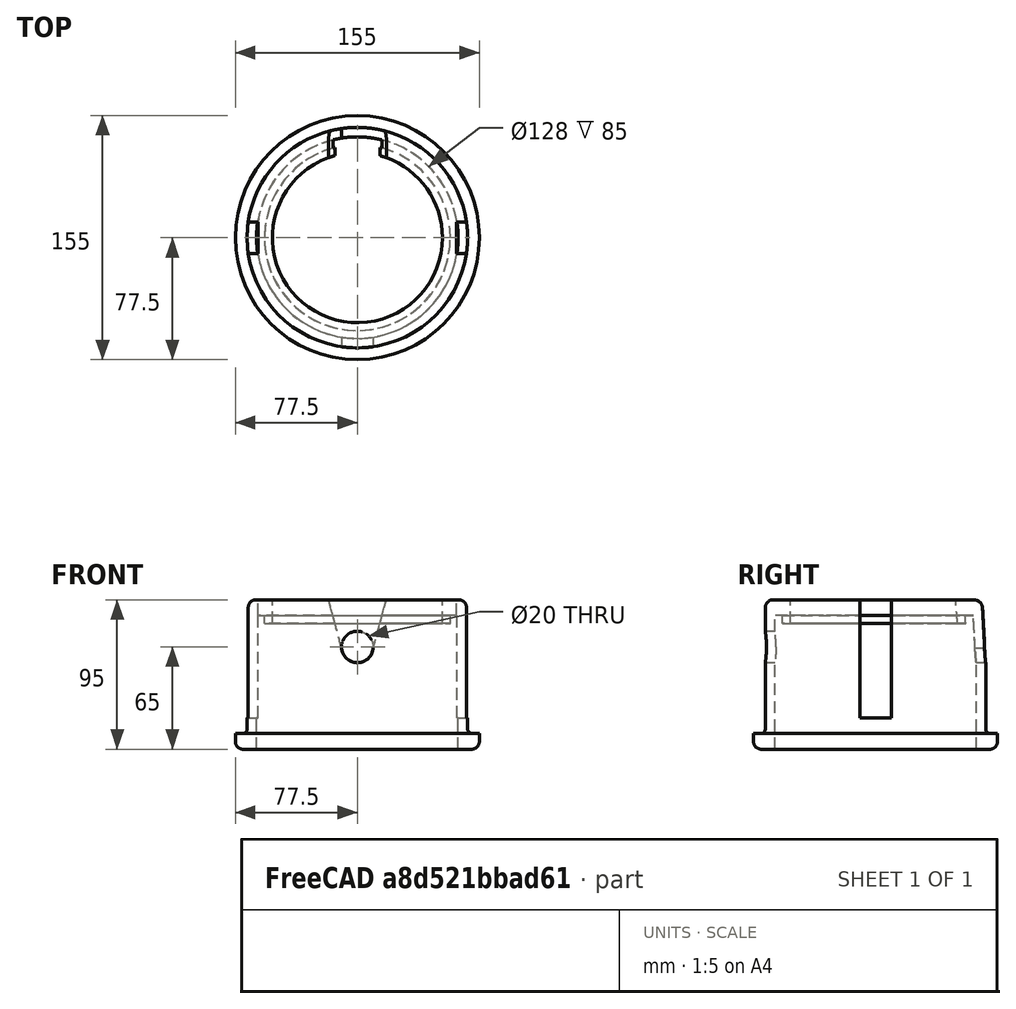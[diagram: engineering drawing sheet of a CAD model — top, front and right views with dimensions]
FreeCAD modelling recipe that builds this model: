
FCSTD DOCUMENT  (FreeCAD 0.15R4671 (Git))
Label: sphere_support_cyls3g
License: All rights reserved
LicenseURL: http://en.wikipedia.org/wiki/All_rights_reserved
objects: Part::Cut×8, Part::Cylinder×6, Part::Box×5, Part::Fillet×3, Part::MultiFuse×2
note: 24 computed .brp shape members not serialized (recipe doc carries the construction recipe); baked Part::Feature solids carry a one-line shape summary decoded from their .brp

FEATURE [Part::Cylinder] Cylinder  label="Base_Cylinder"
  Angle = 360
  Height = 10
  Radius = 77.5
FEATURE [Part::Cylinder] Cylinder001  label="Body_Cylinder"
  Angle = 360
  Height = 90
  Placement = pos=(0,0,5) rot=(0,0,1;0rad)
  Radius = 70
FEATURE [Part::MultiFuse] Fusion  label="Core_Fusion"
  Shapes = -> [Cylinder,Cylinder001]
FEATURE [Part::Cylinder] Cylinder002  label="Inner_Hole"
  Angle = 360
  Height = 85
  Radius = 64
FEATURE [Part::Cut] Cut
  Base = -> Fusion
  Tool = -> Cylinder002
FEATURE [Part::Cylinder] Cylinder003  label="Inner_Lip"
  Angle = 360
  Height = 10
  Placement = pos=(0,0,80) rot=(0,0,1;0rad)
  Radius = 59
FEATURE [Part::MultiFuse] Fusion001
  Shapes = -> [Cut,Cylinder003]
FEATURE [Part::Cylinder] Cylinder004  label="Through_Hole"
  Angle = 360
  Height = 100
  Radius = 54
FEATURE [Part::Cut] Cut001
  Base = -> Fusion001
  Tool = -> Cylinder004
FEATURE [Part::Fillet] Fillet
  Base = -> Cut001
  Edges = 1 edges r=3: [Edge12]
FEATURE [Part::Fillet] Fillet001
  Base = -> Fillet
  Edges = 1 edges r=5: [Edge11]
FEATURE [Part::Fillet] Fillet002
  Base = -> Fillet001
  Edges = 1 edges r=5: [Edge13]
FEATURE [Part::Cylinder] Cylinder005  label="Bearing_Holes"
  Angle = 360
  Height = 180
  Placement = pos=(0,90,65) rot=(1,0,0;1.5708rad)
  Radius = 10
FEATURE [Part::Cut] Cut002
  Base = -> Fillet002
  Tool = -> Cylinder005
FEATURE [Part::Box] Box  label="Bearing_Slot"
  Height = 35
  Length = 20
  Placement = pos=(-10,48,65) rot=(0,0,1;0rad)
  Width = 25
FEATURE [Part::Cut] Cut003
  Base = -> Cut002
  Tool = -> Box
FEATURE [Part::Box] Box001  label="Cube"
  Height = 35
  Length = 10
  Placement = pos=(0,48,65) rot=(0,1,0;0.261799rad)
  Width = 25
FEATURE [Part::Cut] Cut004
  Base = -> Cut003
  Tool = -> Box001
FEATURE [Part::Box] Box002  label="Cube001"
  Height = 35
  Length = 10
  Placement = pos=(-9.95,48,64) rot=(0,-1,0;0.261799rad)
  Width = 25
FEATURE [Part::Cut] Cut005
  Base = -> Cut004
  Tool = -> Box002
FEATURE [Part::Box] Box003  label="Tab_Cut_R"
  Height = 80
  Length = 20
  Placement = pos=(63,-10,20) rot=(0,0,1;0rad)
  Width = 20
FEATURE [Part::Cut] Cut006
  Base = -> Cut005
  Tool = -> Box003
FEATURE [Part::Box] Box004  label="Tab_Cut_L"
  Height = 80
  Length = 20
  Placement = pos=(-83,-10,20) rot=(0,0,1;0rad)
  Width = 20
FEATURE [Part::Cut] Cut007
  Base = -> Cut006
  Tool = -> Box004
